# Revit family: LR1741-03-RD
name_source: partatom
category: Plumbing Fixtures
revit_build: Autodesk Revit MEP 2016 (Build: 20150220_1215(x64)
units: mm (PartAtom-declared; Revit-internal decimal feet)

## family parameters
Cut with Voids When Loaded = No
Host = Face
OmniClass Number = 23.45.05.14.17
OmniClass Title = Showers
Part Type = Normal
Room Calculation Point = No
Round Connector Dimension = Use Diameter
Shared = Yes

## types (2) — shared parameters
-EG Enviro-Glaze (Specify Color) = No
-F Flow Control   2.0GPM (No Longer Available in California) = No
-LRD Less Recessed Soap Dish = No
-TF Transformer, 120VAC to 24VAC (-MVC option only) = No
BRS - Brass Body Valve = No
CW Connection = Yes
EVS1 -  Electronic Valve System Single Temp = No
HW Connection = Yes
LR1741-03-RD - Ligature Resistant Wall Shower = Yes
MT - Metal Template (Only 1 required Per Project) = No
MTP1 - Electronic Valve System PLUS Single Temp = No
MV - Metering Valve, Air-Control Metering = No
MVC1 - Time-Trol Single Temp = No
MVC2 - Time-Trol Hot & Cold = Yes
Manufacturer = Acorn Engineering Company
Material = Stainless Steel-Acorn-Type 304-Satin
PPZ1 - Programmable Piezo Button Single Temp = No
RD - Recessed Soap Dish = Yes
Revised Date = 11/18/2019
SW - Wall Sleeve = No
URL = http://www.acorneng.com
Vent Connection = No
Waste Connection = No

## per-type parameters (varying)
| type | 04 - Hot & Cold Metering | CWFU | Default Elevation | Description | EVS2 -  Electronic Valve System Hot & Cold | EVSP1 - Single Temp, Piezo Button | EVSP2 - Hot & Cold, Piezo Buttons | HWFU | MA2 - Manifolded, 2-stack | MTP2 - Electronic Valve System PLUS Hot & Cold | MTPP1 - Electronic Valve System PLUS Single Temp Piezo Button | MTPP2 - Electronic Valve System PLUS Hot & Cold Piezo Buttons | PPZ2 - Programmable Piezo Buttons Hot & Cold | WFU |
| LR1741-03-RD | No | 0.5 | 63" | Ligature Resistant Wall Shower | No | No | No | 0.5 | No | No | No | No | No | 0 |
| LR1748ADA | Yes | 2 | 55" | Ligature Resistant Wall Shower ADA Compliant | Yes | Yes | Yes | 3 | Yes | Yes | Yes | Yes | Yes | 4 |

note: column(s) folded — value = type name in every type: Model

## geometry (parser evidence)
native form markers: Sweep x17
no freeform markers — native parametric forms only
